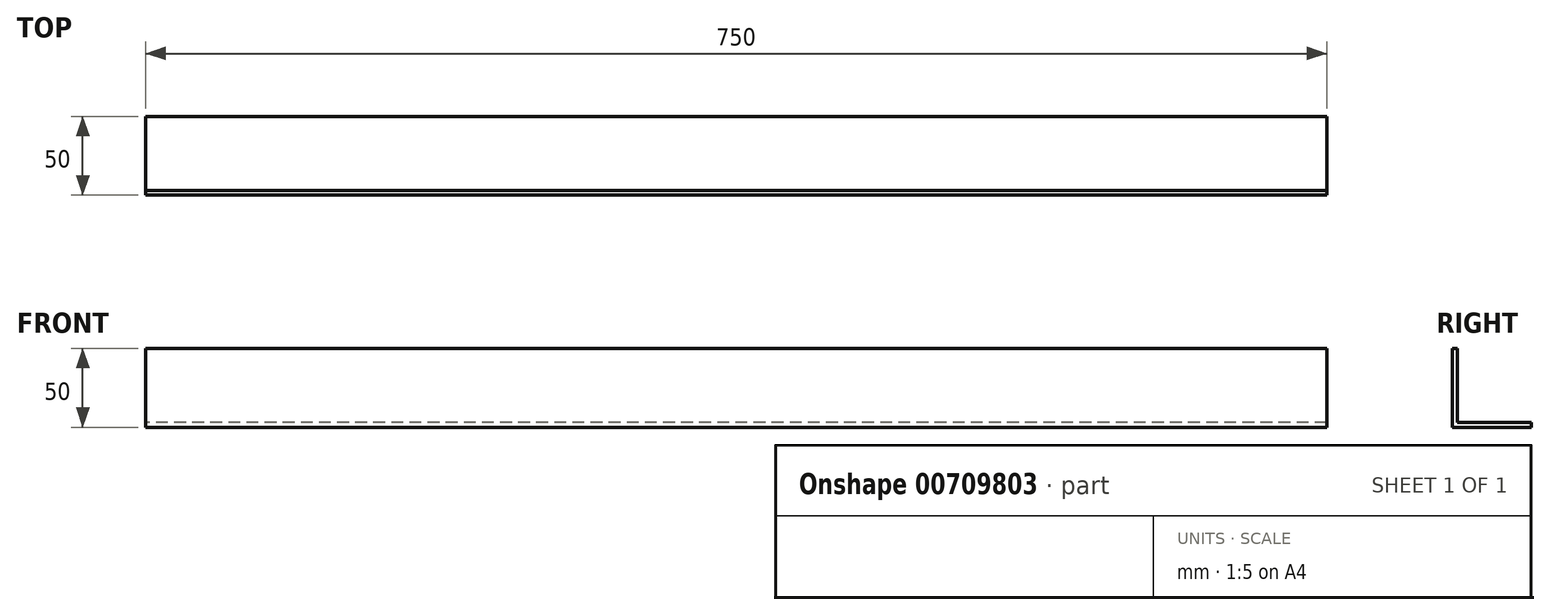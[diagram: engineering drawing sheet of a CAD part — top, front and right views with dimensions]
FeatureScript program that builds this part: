
annotation { "Feature Type Name" : "Feature", "Feature Type Description" : "" }
export const myFeature = defineFeature(function(context is Context, id is Id, definition is map)
    precondition{}
    {
        {
            var Q0;
            Q0=qCreatedBy(makeId("Right.planeOp"),FACE);
            var sketch = newSketch(context, id + "F0", { "sketchPlane" : qUnion([Q0])});
            skLineSegment(sketch, "E0.bottom", {"start": v(-50, 50) * mm, "end": v(-47, 50) * mm});
            skLineSegment(sketch, "E0.top", {"start": v(-50, 0) * mm, "end": v(0, 0) * mm});
            skLineSegment(sketch, "E0.left", {"start": v(-50, 50) * mm, "end": v(-50, 0) * mm});
            skLineSegment(sketch, "E0.right", {"start": v(0, 3) * mm, "end": v(0, 0) * mm});
            skLineSegment(sketch, "E1.2", {"start": v(-47, 50) * mm, "end": v(-47, 3) * mm});
            skLineSegment(sketch, "E1.3", {"start": v(-47, 3) * mm, "end": v(0, 3) * mm});
            skSolve(sketch);
        }
        {
            var Q0;
            Q0=makeQuery(id+"F0.imprint","IMPRINT",FACE,{"disambiguationData":[TD([[makeQuery(id+"F0.imprint","IMPRINT",EDGE,{"derivedFrom":sQuery(id+"F0.wireOp",EDGE,"E0.bottom")}),-1.0]])]});
            extrude(context, id + "F1", {"entities" : qUnion([Q0]), "depth" : 750 * mm, "offsetDistance" : 25 * mm});
        }
    });
